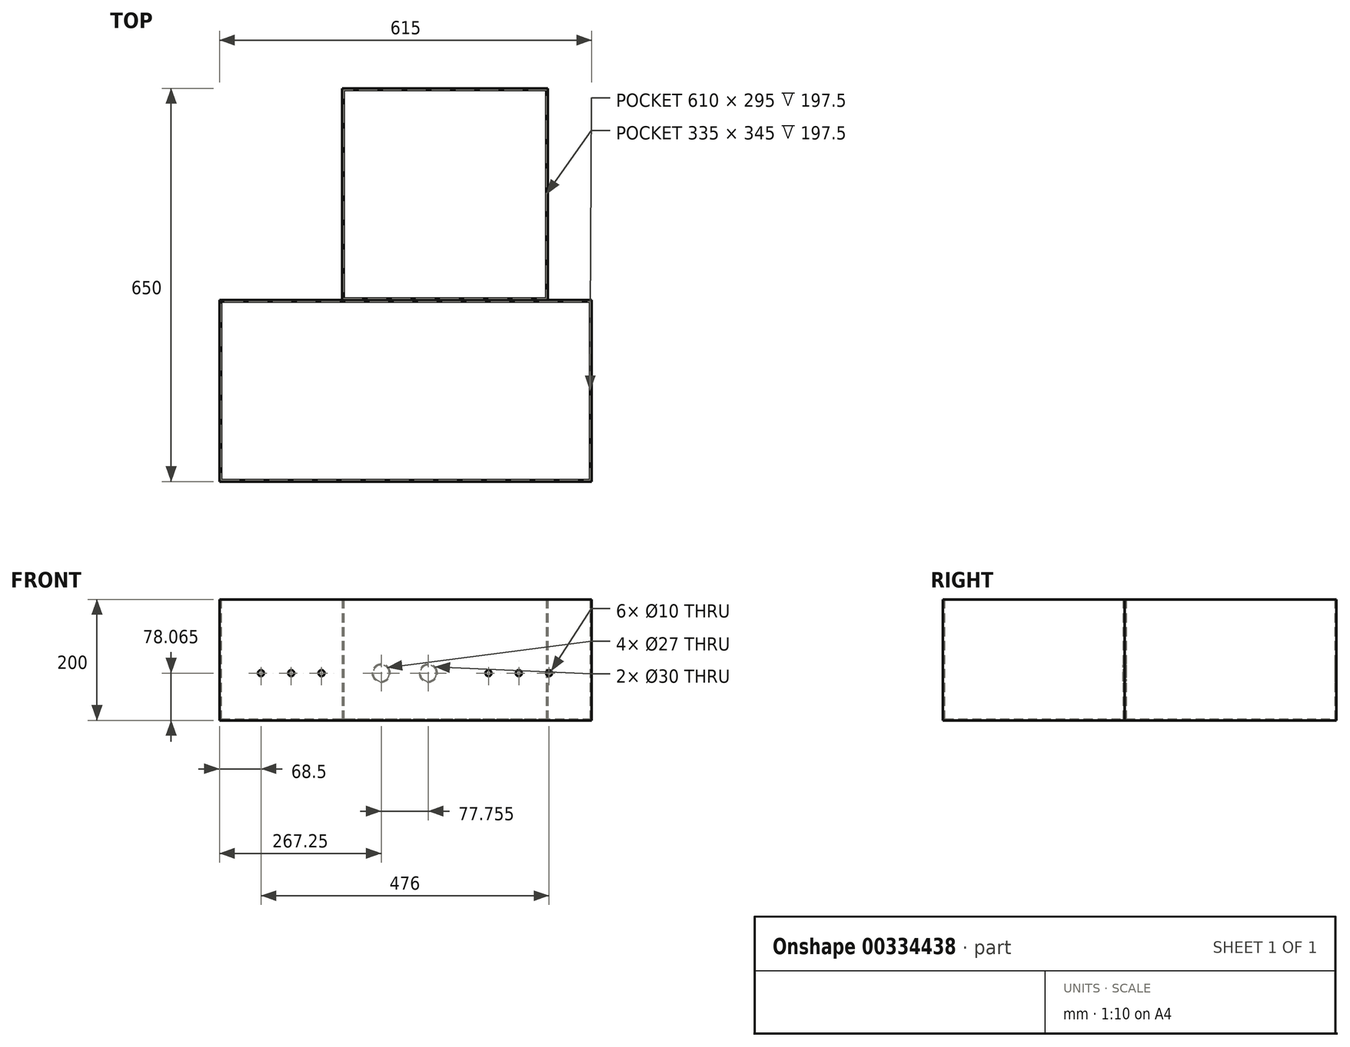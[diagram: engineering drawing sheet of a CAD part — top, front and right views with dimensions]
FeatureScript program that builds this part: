
annotation { "Feature Type Name" : "Feature", "Feature Type Description" : "" }
export const myFeature = defineFeature(function(context is Context, id is Id, definition is map)
    precondition{}
    {
        {
            var Q0;
            Q0=qCreatedBy(makeId("Top.planeOp"),FACE);
            var sketch = newSketch(context, id + "F0", { "sketchPlane" : qUnion([Q0])});
            skLineSegment(sketch, "E0.bottom", {"start": v(-465, 150) * mm, "end": v(465, 150) * mm});
            skLineSegment(sketch, "E0.top", {"start": v(-465, -150) * mm, "end": v(465, -150) * mm});
            skLineSegment(sketch, "E0.left", {"start": v(-465, 150) * mm, "end": v(-465, -150) * mm});
            skLineSegment(sketch, "E0.right", {"start": v(465, 150) * mm, "end": v(465, -150) * mm});
            skPoint(sketch, "E0.middle", {"position": v(0, 0) * mm});
            skSolve(sketch);
        }
        {
            var Q0;
            Q0=qCreatedBy(makeId("Top.planeOp"),FACE);
            var sketch = newSketch(context, id + "F1", { "sketchPlane" : qUnion([Q0])});
            skLineSegment(sketch, "E1.bottom", {"start": v(-105, 150) * mm, "end": v(235, 150) * mm});
            skLineSegment(sketch, "E1.top", {"start": v(-105, 500) * mm, "end": v(235, 500) * mm});
            skLineSegment(sketch, "E1.left", {"start": v(-105, 150) * mm, "end": v(-105, 500) * mm});
            skLineSegment(sketch, "E1.right", {"start": v(235, 150) * mm, "end": v(235, 500) * mm});
            skLineSegment(sketch, "E2", {"start": v(-105, 150) * mm, "end": v(-105, 32.22) * mm, "construction": true});
            skLineSegment(sketch, "E3", {"start": v(-105, 32.22) * mm, "end": v(-465, 32.22) * mm, "construction": true});
            skLineSegment(sketch, "E4", {"start": v(235, 150) * mm, "end": v(235, 22) * mm, "construction": true});
            skLineSegment(sketch, "E5", {"start": v(235, 22) * mm, "end": v(465, 22) * mm, "construction": true});
            skSolve(sketch);
        }
        {
            var Q0;
            Q0=makeQuery(id+"F0.imprint","IMPRINT",FACE,{"disambiguationData":[TD([[makeQuery(id+"F0.imprint","IMPRINT",EDGE,{"derivedFrom":sQuery(id+"F0.wireOp",EDGE,"E0.bottom")}),-1.0]])]});
            extrude(context, id + "F2", {"entities" : qUnion([Q0]), "depth" : 200 * mm});
        }
        {
            var Q0;
            Q0=makeQuery(id+"F2.opExtrude","CAP_FACE",FACE,{"disambiguationData":[OSD([sQuery(id+"F0.wireOp",EDGE,"E0.bottom"),sQuery(id+"F0.wireOp",EDGE,"E0.top"),sQuery(id+"F0.wireOp",EDGE,"E0.left"),sQuery(id+"F0.wireOp",EDGE,"E0.right")])],"isStart":false});
            shell(context, id + "F3", {"entities" : qUnion([Q0]), "thickness" : 2.5 * mm});
        }
        {
            var Q0;
            Q0=makeQuery(id+"F1.imprint","IMPRINT",FACE,{"disambiguationData":[TD([[makeQuery(id+"F1.imprint","IMPRINT",EDGE,{"derivedFrom":sQuery(id+"F1.wireOp",EDGE,"E1.bottom")}),1.0]])]});
            extrude(context, id + "F4", {"entities" : qUnion([Q0]), "depth" : 200 * mm});
        }
        {
            var Q0;
            Q0=makeQuery(id+"F4.opExtrude","CAP_FACE",FACE,{"disambiguationData":[OSD([sQuery(id+"F1.wireOp",EDGE,"E1.bottom"),sQuery(id+"F1.wireOp",EDGE,"E1.top"),sQuery(id+"F1.wireOp",EDGE,"E1.left"),sQuery(id+"F1.wireOp",EDGE,"E1.right")])],"isStart":false});
            shell(context, id + "F5", {"entities" : qUnion([Q0]), "thickness" : 2.5 * mm});
        }
        {
            var Q0;
            Q0=makeQuery(id+"F2.opExtrude","SWEPT_FACE",FACE,{"disambiguationData":[OSD([sQuery(id+"F0.wireOp",EDGE,"E0.top")])]});
            var sketch = newSketch(context, id + "F6", { "sketchPlane" : qUnion([Q0])});
            skLineSegment(sketch, "E6", {"start": v(-450, 200) * mm, "end": v(-450, 0) * mm, "construction": true});
            skLineSegment(sketch, "E7", {"start": v(450, 200) * mm, "end": v(450, 0) * mm, "construction": true});
            skLineSegment(sketch, "E8", {"start": v(450, 100) * mm, "end": v(465, 100) * mm, "construction": true});
            skLineSegment(sketch, "E9", {"start": v(-450, 100) * mm, "end": v(-465, 100) * mm, "construction": true});
            skLineSegment(sketch, "E10", {"start": v(-450, 100) * mm, "end": v(450, 100) * mm, "construction": true});
            skCircle(sketch, "E11", {"center": v(387, 78.06) * mm, "radius": 5 * mm});
            skLineSegment(sketch, "E12", {"start": v(387, 2.5) * mm, "end": v(387, 78.06) * mm, "construction": true});
            skLineSegment(sketch, "E13", {"start": v(450, 78.06) * mm, "end": v(387, 78.06) * mm, "construction": true});
            skCircle(sketch, "E14.1.0.0", {"center": v(337, 78.06) * mm, "radius": 5 * mm});
            skCircle(sketch, "E14.2.0.0", {"center": v(287, 78.06) * mm, "radius": 5 * mm});
            skCircle(sketch, "E14.3.0.0", {"center": v(237, 78.06) * mm, "radius": 5 * mm});
            skCircle(sketch, "E14.4.0.0", {"center": v(187, 78.06) * mm, "radius": 5 * mm});
            skCircle(sketch, "E14.5.0.0", {"center": v(137, 78.06) * mm, "radius": 5 * mm});
            skLineSegment(sketch, "E14.direction1", {"start": v(387, 78.06) * mm, "end": v(337, 78.06) * mm, "construction": true});
            skLineSegment(sketch, "E15", {"start": v(0, 0) * mm, "end": v(0, 200) * mm, "construction": true});
            skLineSegment(sketch, "E16", {"start": v(337, 78.06) * mm, "end": v(37.5, 78.06) * mm, "construction": true});
            skCircle(sketch, "E17", {"center": v(37.5, 78.06) * mm, "radius": 13.5 * mm});
            skLineSegment(sketch, "E18", {"start": v(37.5, 78.06) * mm, "end": v(37.5, 25.26) * mm, "construction": true});
            skLineSegment(sketch, "E19", {"start": v(37.5, 25.26) * mm, "end": v(450, 25.26) * mm, "construction": true});
            skCircle(sketch, "E20.MirrorC", {"center": v(-37.5, 78.06) * mm, "radius": 13.5 * mm});
            skCircle(sketch, "E21", {"center": v(-389, 78.06) * mm, "radius": 5 * mm});
            skLineSegment(sketch, "E22", {"start": v(-389, 78.06) * mm, "end": v(-450, 78.06) * mm, "construction": true});
            skCircle(sketch, "E23.1.0.0", {"center": v(-339, 78.06) * mm, "radius": 5 * mm});
            skCircle(sketch, "E23.2.0.0", {"center": v(-289, 78.06) * mm, "radius": 5 * mm});
            skCircle(sketch, "E23.3.0.0", {"center": v(-239, 78.06) * mm, "radius": 5 * mm});
            skCircle(sketch, "E23.4.0.0", {"center": v(-189, 78.06) * mm, "radius": 5 * mm});
            skCircle(sketch, "E23.5.0.0", {"center": v(-139, 78.06) * mm, "radius": 5 * mm});
            skLineSegment(sketch, "E23.direction1", {"start": v(-389, 78.06) * mm, "end": v(-339, 78.06) * mm, "construction": true});
            skSolve(sketch);
        }
        {
            var Q0;
            Q0=makeQuery(id+"F6.imprint","IMPRINT",FACE,{"disambiguationData":[TD([[makeQuery(id+"F6.imprint","IMPRINT",EDGE,{"derivedFrom":sQuery(id+"F6.wireOp",EDGE,"2fb40452-a07c-48d1-afae-638b5858da225.MirrorC")}),-1.0]])]});
            var Q1;
            Q1=makeQuery(id+"F6.imprint","IMPRINT",FACE,{"disambiguationData":[TD([[makeQuery(id+"F6.imprint","IMPRINT",EDGE,{"derivedFrom":sQuery(id+"F6.wireOp",EDGE,"2fb40452-a07c-48d1-afae-638b5858da224.MirrorC")}),-1.0]])]});
            var Q2;
            Q2=makeQuery(id+"F6.imprint","IMPRINT",FACE,{"disambiguationData":[TD([[makeQuery(id+"F6.imprint","IMPRINT",EDGE,{"derivedFrom":sQuery(id+"F6.wireOp",EDGE,"2fb40452-a07c-48d1-afae-638b5858da223.MirrorC")}),-1.0]])]});
            var Q3;
            Q3=makeQuery(id+"F6.imprint","IMPRINT",FACE,{"disambiguationData":[TD([[makeQuery(id+"F6.imprint","IMPRINT",EDGE,{"derivedFrom":sQuery(id+"F6.wireOp",EDGE,"2fb40452-a07c-48d1-afae-638b5858da222.MirrorC")}),-1.0]])]});
            var Q4;
            Q4=makeQuery(id+"F6.imprint","IMPRINT",FACE,{"disambiguationData":[TD([[makeQuery(id+"F6.imprint","IMPRINT",EDGE,{"derivedFrom":sQuery(id+"F6.wireOp",EDGE,"2fb40452-a07c-48d1-afae-638b5858da221.MirrorC")}),-1.0]])]});
            var Q5;
            Q5=makeQuery(id+"F6.imprint","IMPRINT",FACE,{"disambiguationData":[TD([[makeQuery(id+"F6.imprint","IMPRINT",EDGE,{"derivedFrom":sQuery(id+"F6.wireOp",EDGE,"2fb40452-a07c-48d1-afae-638b5858da220.MirrorC")}),-1.0]])]});
            var Q6;
            Q6=makeQuery(id+"F6.imprint","IMPRINT",FACE,{"disambiguationData":[TD([[makeQuery(id+"F6.imprint","IMPRINT",EDGE,{"derivedFrom":sQuery(id+"F6.wireOp",EDGE,"E14.5.0.0")}),1.0]])]});
            var Q7;
            Q7=makeQuery(id+"F6.imprint","IMPRINT",FACE,{"disambiguationData":[TD([[makeQuery(id+"F6.imprint","IMPRINT",EDGE,{"derivedFrom":sQuery(id+"F6.wireOp",EDGE,"E14.4.0.0")}),1.0]])]});
            var Q8;
            Q8=makeQuery(id+"F6.imprint","IMPRINT",FACE,{"disambiguationData":[TD([[makeQuery(id+"F6.imprint","IMPRINT",EDGE,{"derivedFrom":sQuery(id+"F6.wireOp",EDGE,"E14.3.0.0")}),1.0]])]});
            var Q9;
            Q9=makeQuery(id+"F6.imprint","IMPRINT",FACE,{"disambiguationData":[TD([[makeQuery(id+"F6.imprint","IMPRINT",EDGE,{"derivedFrom":sQuery(id+"F6.wireOp",EDGE,"E11")}),1.0]])]});
            var Q10;
            Q10=makeQuery(id+"F6.imprint","IMPRINT",FACE,{"disambiguationData":[TD([[makeQuery(id+"F6.imprint","IMPRINT",EDGE,{"derivedFrom":sQuery(id+"F6.wireOp",EDGE,"E14.1.0.0")}),1.0]])]});
            var Q11;
            Q11=makeQuery(id+"F6.imprint","IMPRINT",FACE,{"disambiguationData":[TD([[makeQuery(id+"F6.imprint","IMPRINT",EDGE,{"derivedFrom":sQuery(id+"F6.wireOp",EDGE,"E23.5.0.0")}),1.0]])]});
            var Q12;
            Q12=makeQuery(id+"F6.imprint","IMPRINT",FACE,{"disambiguationData":[TD([[makeQuery(id+"F6.imprint","IMPRINT",EDGE,{"derivedFrom":sQuery(id+"F6.wireOp",EDGE,"E23.4.0.0")}),1.0]])]});
            var Q13;
            Q13=makeQuery(id+"F6.imprint","IMPRINT",FACE,{"disambiguationData":[TD([[makeQuery(id+"F6.imprint","IMPRINT",EDGE,{"derivedFrom":sQuery(id+"F6.wireOp",EDGE,"E23.3.0.0")}),1.0]])]});
            var Q14;
            Q14=makeQuery(id+"F6.imprint","IMPRINT",FACE,{"disambiguationData":[TD([[makeQuery(id+"F6.imprint","IMPRINT",EDGE,{"derivedFrom":sQuery(id+"F6.wireOp",EDGE,"E23.1.0.0")}),1.0]])]});
            var Q15;
            Q15=makeQuery(id+"F6.imprint","IMPRINT",FACE,{"disambiguationData":[TD([[makeQuery(id+"F6.imprint","IMPRINT",EDGE,{"derivedFrom":sQuery(id+"F6.wireOp",EDGE,"E21")}),1.0]])]});
            extrude(context, id + "F7", {"entities" : qUnion([Q0, Q1, Q2, Q3, Q4, Q5, Q6, Q7, Q8, Q9, Q10, Q11, Q12, Q13, Q14, Q15]), "operationType" : NewBodyOperationType.REMOVE, "oppositeDirection" : true, "depth" : 25 * mm});
        }
        {
            var Q0;
            Q0=makeQuery(id+"F3.opShell","OFFSET_FACE",FACE,{"disambiguationData":[OSD([sQuery(id+"F0.wireOp",EDGE,"E0.bottom")])]});
            var sketch = newSketch(context, id + "F8", { "sketchPlane" : qUnion([Q0])});
            skCircle(sketch, "E24", {"center": v(37.5, 78.06) * mm, "radius": 13.5 * mm});
            skCircle(sketch, "E25", {"center": v(-40.25, 78.06) * mm, "radius": 13.5 * mm});
            skLineSegment(sketch, "E26", {"start": v(37.5, 78.06) * mm, "end": v(-40.25, 78.06) * mm, "construction": true});
            skSolve(sketch);
        }
        {
            var Q0;
            Q0=qSketchRegion(id+"F8",true);
            extrude(context, id + "F9", {"entities" : qUnion([Q0]), "operationType" : NewBodyOperationType.REMOVE, "oppositeDirection" : true, "depth" : 25 * mm});
        }
        {
            var Q0;
            Q0=makeQuery(id+"F4.opExtrude","SWEPT_FACE",FACE,{"disambiguationData":[OSD([sQuery(id+"F1.wireOp",EDGE,"E1.top")])]});
            var sketch = newSketch(context, id + "F10", { "sketchPlane" : qUnion([Q0])});
            skCircle(sketch, "E27", {"center": v(-37.5, 78.06) * mm, "radius": 15 * mm});
            skCircle(sketch, "E28", {"center": v(40.25, 78.06) * mm, "radius": 15 * mm});
            skSolve(sketch);
        }
        {
            var Q0;
            Q0=qSketchRegion(id+"F10",true);
            extrude(context, id + "F11", {"entities" : qUnion([Q0]), "operationType" : NewBodyOperationType.REMOVE, "oppositeDirection" : true, "depth" : 25 * mm});
        }
        {
            var Q0;
            Q0=makeQuery(id+"F2.opExtrude","SWEPT_FACE",FACE,{"disambiguationData":[OSD([sQuery(id+"F0.wireOp",EDGE,"E0.left")])]});
            extrude(context, id + "F12", {"entities" : qUnion([Q0]), "operationType" : NewBodyOperationType.REMOVE, "oppositeDirection" : true, "depth" : 160 * mm});
        }
        {
            var Q0;
            Q0=makeQuery(id+"F2.opExtrude","SWEPT_FACE",FACE,{"disambiguationData":[OSD([sQuery(id+"F0.wireOp",EDGE,"E0.right")])]});
            extrude(context, id + "F13", {"entities" : qUnion([Q0]), "operationType" : NewBodyOperationType.REMOVE, "oppositeDirection" : true, "depth" : 160 * mm});
        }
        {
            var Q0;
            Q0=makeQuery(id+"F13.boolean.opBoolean","COPY",FACE,{"derivedFrom":makeQuery(id+"F13.opExtrude","CAP_FACE",FACE,{"disambiguationData":[OSD([sQuery(id+"F0.wireOp",EDGE,"E0.right")])],"isStart":false})});
            var sketch = newSketch(context, id + "F14", { "sketchPlane" : qUnion([Q0])});
            skLineSegment(sketch, "E29.bottom", {"start": v(-150, 0) * mm, "end": v(150, 0) * mm});
            skLineSegment(sketch, "E29.top", {"start": v(-150, 200) * mm, "end": v(150, 200) * mm});
            skLineSegment(sketch, "E29.left", {"start": v(-150, 0) * mm, "end": v(-150, 200) * mm});
            skLineSegment(sketch, "E29.right", {"start": v(150, 0) * mm, "end": v(150, 200) * mm});
            skSolve(sketch);
        }
        {
            var Q0;
            Q0 = qSketchRegion(id + "F14", true);
            extrude(context, id + "F15", {"entities" : qUnion([Q0]), "operationType" : NewBodyOperationType.ADD, "depth" : 2.5 * mm});
        }
        {
            var Q0;
            Q0=makeQuery(id+"F12.boolean.opBoolean","COPY",FACE,{"derivedFrom":makeQuery(id+"F12.opExtrude","CAP_FACE",FACE,{"disambiguationData":[OSD([sQuery(id+"F0.wireOp",EDGE,"E0.left")])],"isStart":false})});
            var sketch = newSketch(context, id + "F16", { "sketchPlane" : qUnion([Q0])});
            skLineSegment(sketch, "E30.bottom", {"start": v(-150, 0) * mm, "end": v(150, 0) * mm});
            skLineSegment(sketch, "E30.top", {"start": v(-150, 200) * mm, "end": v(150, 200) * mm});
            skLineSegment(sketch, "E30.left", {"start": v(-150, 0) * mm, "end": v(-150, 200) * mm});
            skLineSegment(sketch, "E30.right", {"start": v(150, 0) * mm, "end": v(150, 200) * mm});
            skSolve(sketch);
        }
        {
            var Q0;
            Q0 = qSketchRegion(id + "F16", true);
            extrude(context, id + "F17", {"entities" : qUnion([Q0]), "operationType" : NewBodyOperationType.ADD, "depth" : 2.5 * mm});
        }
    });
